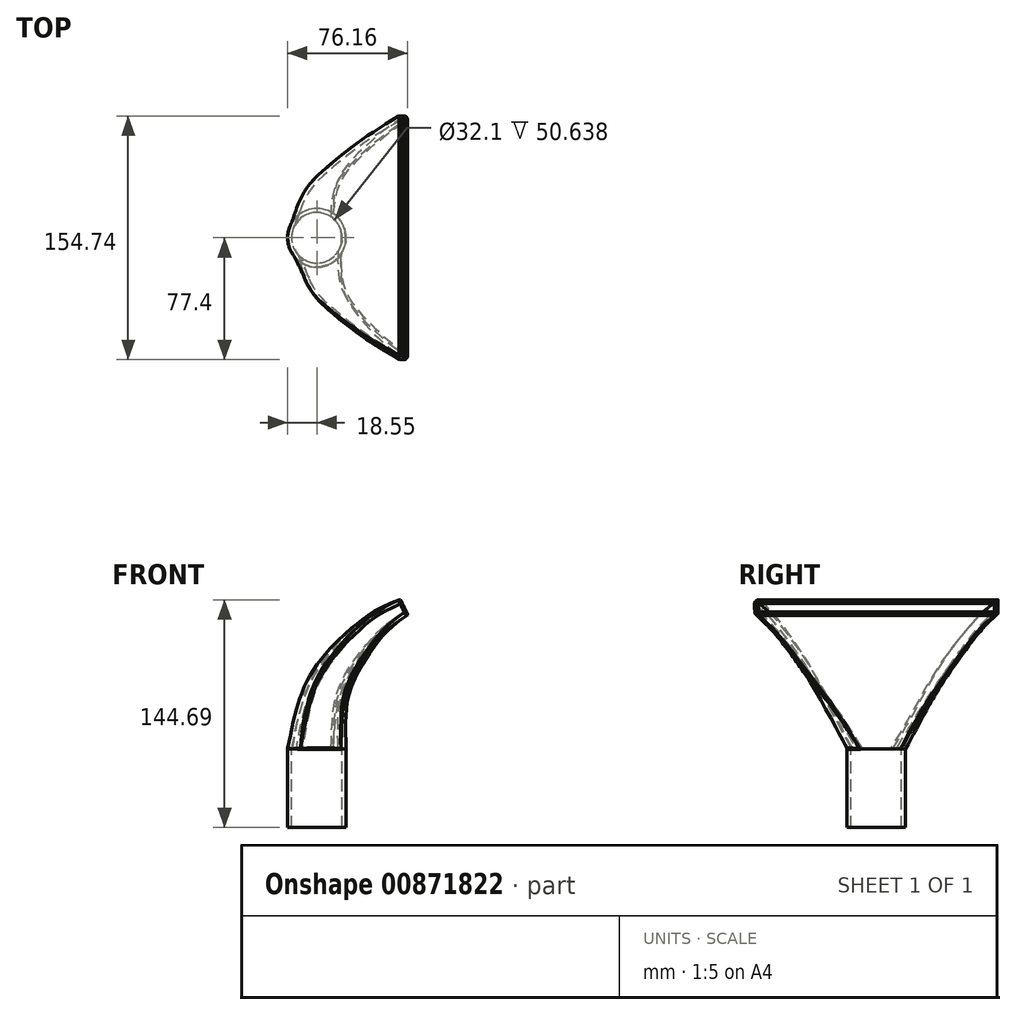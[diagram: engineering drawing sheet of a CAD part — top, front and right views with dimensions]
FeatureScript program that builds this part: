
annotation { "Feature Type Name" : "Feature", "Feature Type Description" : "" }
export const myFeature = defineFeature(function(context is Context, id is Id, definition is map)
    precondition{}
    {
        {
            var Q0;
            Q0=qCreatedBy(makeId("Front.planeOp"),FACE);
            var sketch = newSketch(context, id + "F0", { "sketchPlane" : qUnion([Q0])});
            skLineSegment(sketch, "E0", {"start": v(0, 0) * mm, "end": v(0, 50) * mm});
            skFitSpline(sketch, "E1", {"points": [v(0, 50) * mm, v(5.1, 83.3) * mm, v(17.58, 106.9) * mm, v(39.8, 130.5) * mm, v(55.5, 140) * mm], "startDerivative": vector(11.63, 127.23) * mm, "endDerivative": vector(74.52, 35.9) * mm});
            skSolve(sketch);
        }
        {
            var Q0;
            Q0=qCreatedBy(makeId("Top.planeOp"),FACE);
            cPlane(context, id + "F1", {"entities" : qUnion([Q0]), "cplaneType" : CPlaneType.OFFSET, "offset" : 50 * mm, "width" : 150 * mm, "height" : 150 * mm});
        }
        {
            var Q0;
            Q0=qCreatedBy(id+"F1.planeOp",FACE);
            var sketch = newSketch(context, id + "F2", { "sketchPlane" : qUnion([Q0])});
            skCircle(sketch, "E2", {"center": v(0, 0) * mm, "radius": 18.55 * mm});
            skSolve(sketch);
        }
        {
            var Q0;
            Q0=sQuery(id+"F0.wireOp",EDGE,"E1");
            var Q1;
            Q1=sQuery(id+"F0.wireOp",VERTEX,"E1.end");
            cPlane(context, id + "F3", {"entities" : qUnion([Q0, Q1]), "cplaneType" : CPlaneType.CURVE_POINT, "offset" : 25 * mm, "width" : 150 * mm, "height" : 150 * mm});
        }
        {
            var Q0;
            Q0=qCreatedBy(id+"F3.planeOp",FACE);
            var sketch = newSketch(context, id + "F4", { "sketchPlane" : qUnion([Q0])});
            skLineSegment(sketch, "E3.bottom", {"start": v(78, 107.53) * mm, "end": v(-78, 107.53) * mm});
            skLineSegment(sketch, "E3.top", {"start": v(78, 96.53) * mm, "end": v(-78, 96.53) * mm});
            skLineSegment(sketch, "E3.left", {"start": v(78, 107.53) * mm, "end": v(78, 96.53) * mm});
            skLineSegment(sketch, "E3.right", {"start": v(-78, 107.53) * mm, "end": v(-78, 96.53) * mm});
            skPoint(sketch, "E3.middle", {"position": v(0, 102.03) * mm});
            skSolve(sketch);
        }
        {
            var Q0;
            Q0=sQuery(id+"F0.wireOp",EDGE,"E1");
            var Q1;
            Q1=makeQuery(id+"F2.imprint","IMPRINT",FACE,{"disambiguationData":[TD([[makeQuery(id+"F2.imprint","IMPRINT",EDGE,{"derivedFrom":sQuery(id+"F2.wireOp",EDGE,"E2")}),1.0]])]});
            var Q2;
            Q2=makeQuery(id+"F4.imprint","IMPRINT",FACE,{"disambiguationData":[TD([[makeQuery(id+"F4.imprint","IMPRINT",EDGE,{"derivedFrom":sQuery(id+"F4.wireOp",EDGE,"E3.bottom")}),1.0]])]});
            loft(context, id + "F5", {"addSections" : true, "spine" : qUnion([Q0]), "sectionCount" : 5, "sheetProfilesArray" : [{ "sheetProfileEntities" : qUnion([Q1]) }, { "sheetProfileEntities" : qUnion([Q2]) }]});
        }
        {
            var Q0;
            Q0=makeQuery(id+"F2.imprint","IMPRINT",FACE,{"disambiguationData":[TD([[makeQuery(id+"F2.imprint","IMPRINT",EDGE,{"derivedFrom":sQuery(id+"F2.wireOp",EDGE,"E2")}),1.0]])]});
            extrude(context, id + "F6", {"entities" : qUnion([Q0]), "operationType" : NewBodyOperationType.ADD, "oppositeDirection" : true, "depth" : 50 * mm, "offsetDistance" : 25 * mm});
        }
        {
            var Q0;
            Q0=makeQuery(id+"F5.opLoft","CAP_FACE",FACE,{"disambiguationData":[OSD([makeQuery(id+"F4.imprint","IMPRINT",FACE,{"disambiguationData":[TD([[makeQuery(id+"F4.imprint","IMPRINT",EDGE,{"derivedFrom":sQuery(id+"F4.wireOp",EDGE,"E3.bottom")}),1.0]])]})])],"isStart":true});
            var Q1;
            Q1=makeQuery(id+"F6.opExtrude","CAP_FACE",FACE,{"disambiguationData":[OSD([sQuery(id+"F2.wireOp",EDGE,"E2")])],"isStart":false});
            shell(context, id + "F7", {"entities" : qUnion([Q0, Q1]), "thickness" : 2.5 * mm});
        }
        {
            var Q0;
            Q0=makeQuery(id+"F5.opLoft","SWEPT_EDGE",EDGE,{"disambiguationData":[OSD([sQuery(id+"F2.wireOp",EDGE,"E2"),sQuery(id+"F4.wireOp",EDGE,"E3.bottom"),sQuery(id+"F4.wireOp",EDGE,"E3.left"),sQuery(id+"F4.wireOp",EDGE,"E3.right")])]});
            var Q1;
            Q1=makeQuery(id+"F5.opLoft","SWEPT_EDGE",EDGE,{"disambiguationData":[OSD([sQuery(id+"F2.wireOp",EDGE,"E2"),sQuery(id+"F4.wireOp",EDGE,"E3.bottom"),sQuery(id+"F4.wireOp",EDGE,"E3.top"),sQuery(id+"F4.wireOp",EDGE,"E3.right")])]});
            var Q2;
            Q2=makeQuery(id+"F5.opLoft","SWEPT_EDGE",EDGE,{"disambiguationData":[OSD([sQuery(id+"F2.wireOp",EDGE,"E2"),sQuery(id+"F4.wireOp",EDGE,"E3.bottom"),sQuery(id+"F4.wireOp",EDGE,"E3.top"),sQuery(id+"F4.wireOp",EDGE,"E3.left")])]});
            var Q3;
            Q3=makeQuery(id+"F5.opLoft","SWEPT_EDGE",EDGE,{"disambiguationData":[OSD([sQuery(id+"F4.wireOp",EDGE,"E3.bottom"),sQuery(id+"F4.wireOp",EDGE,"E3.top"),sQuery(id+"F4.wireOp",EDGE,"E3.left")])]});
            fillet(context, id + "F8", {"entities" : qUnion([Q0, Q1, Q2, Q3]), "radius" : 2.5 * mm, "tangentPropagation" : true, "allowEdgeOverflow" : false});
        }
        {
            var Q0;
            Q0=makeQuery(id+"F5.opLoft","MID_CAP_EDGE",EDGE,{"disambiguationData":[OSD([sQuery(id+"F4.wireOp",EDGE,"E3.bottom"),sQuery(id+"F4.wireOp",EDGE,"E3.left"),sQuery(id+"F4.wireOp",EDGE,"E3.right")])],"capPos":1.0});
            var Q1;
            Q1=makeQuery(id+"F5.opLoft","CAP_FACE",FACE,{"disambiguationData":[OSD([makeQuery(id+"F4.imprint","IMPRINT",FACE,{"disambiguationData":[TD([[makeQuery(id+"F4.imprint","IMPRINT",EDGE,{"derivedFrom":sQuery(id+"F4.wireOp",EDGE,"E3.bottom")}),1.0]])]})])],"isStart":true});
            fillet(context, id + "F9", {"entities" : qUnion([Q0, Q1]), "radius" : 1 * mm, "tangentPropagation" : true, "allowEdgeOverflow" : false});
        }
        {
            var Q0;
            {var subQ0=sQuery(id+"F2.wireOp",EDGE,"E2");Q0=makeQuery(id+"F6.boolean.opBoolean","MERGE",EDGE,{"derivedFrom":[makeQuery(id+"F5.opLoft","MID_CAP_EDGE",EDGE,{"disambiguationData":[OSD([subQ0,sQuery(id+"F4.wireOp",EDGE,"E3.bottom"),sQuery(id+"F4.wireOp",EDGE,"E3.left"),sQuery(id+"F4.wireOp",EDGE,"E3.right")]),OD(0.0)],"capPos":0.0}),makeQuery(id+"F6.opExtrude","CAP_EDGE",EDGE,{"disambiguationData":[OSD([subQ0])],"isStart":true})]});}
            var Q1;
            {var subQ0=sQuery(id+"F2.wireOp",EDGE,"E2");Q1=makeQuery(id+"F6.boolean.opBoolean","MERGE",EDGE,{"derivedFrom":[makeQuery(id+"F5.opLoft","MID_CAP_EDGE",EDGE,{"disambiguationData":[OSD([subQ0,sQuery(id+"F4.wireOp",EDGE,"E3.bottom"),sQuery(id+"F4.wireOp",EDGE,"E3.top"),sQuery(id+"F4.wireOp",EDGE,"E3.left")]),OD(0.0)],"capPos":0.0}),makeQuery(id+"F6.opExtrude","CAP_EDGE",EDGE,{"disambiguationData":[OSD([subQ0])],"isStart":true})]});}
            var Q2;
            {var subQ0=sQuery(id+"F2.wireOp",EDGE,"E2");Q2=makeQuery(id+"F6.boolean.opBoolean","MERGE",EDGE,{"derivedFrom":[makeQuery(id+"F5.opLoft","MID_CAP_EDGE",EDGE,{"disambiguationData":[OSD([subQ0,sQuery(id+"F4.wireOp",EDGE,"E3.bottom"),sQuery(id+"F4.wireOp",EDGE,"E3.left"),sQuery(id+"F4.wireOp",EDGE,"E3.right")]),OD(1.0)],"capPos":0.0}),makeQuery(id+"F6.opExtrude","CAP_EDGE",EDGE,{"disambiguationData":[OSD([subQ0])],"isStart":true})]});}
            fillet(context, id + "F10", {"entities" : qUnion([Q0, Q1, Q2]), "radius" : 2 * mm, "tangentPropagation" : true, "allowEdgeOverflow" : false});
        }
    });
